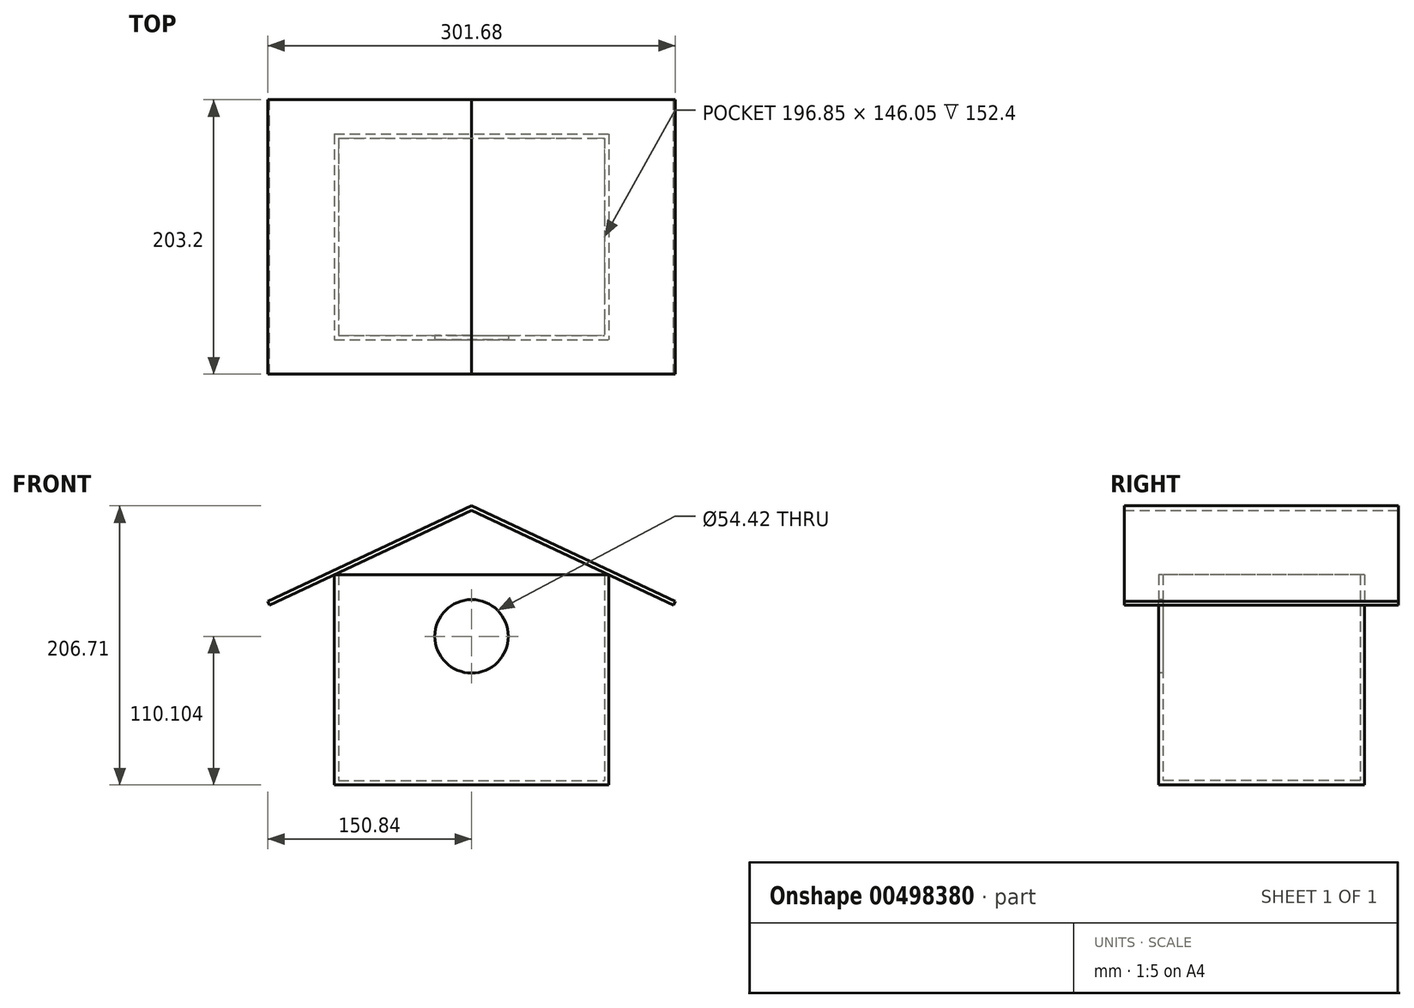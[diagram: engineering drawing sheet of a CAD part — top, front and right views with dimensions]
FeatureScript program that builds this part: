
annotation { "Feature Type Name" : "Feature", "Feature Type Description" : "" }
export const myFeature = defineFeature(function(context is Context, id is Id, definition is map)
    precondition{}
    {
        {
            var Q0;
            Q0=qCreatedBy(makeId("Top.planeOp"),FACE);
            var sketch = newSketch(context, id + "F0", { "sketchPlane" : qUnion([Q0])});
            skLineSegment(sketch, "E0.bottom", {"start": v(-101.6, 76.2) * mm, "end": v(101.6, 76.2) * mm});
            skLineSegment(sketch, "E0.top", {"start": v(-101.6, -76.2) * mm, "end": v(101.6, -76.2) * mm});
            skLineSegment(sketch, "E0.left", {"start": v(-101.6, 76.2) * mm, "end": v(-101.6, -76.2) * mm});
            skLineSegment(sketch, "E0.right", {"start": v(101.6, 76.2) * mm, "end": v(101.6, -76.2) * mm});
            skLineSegment(sketch, "E1", {"start": v(-101.6, 76.2) * mm, "end": v(101.6, -76.2) * mm, "construction": true});
            skSolve(sketch);
        }
        {
            var Q0;
            Q0 = qSketchRegion(id + "F0", true);
            extrude(context, id + "F1", {"entities" : qUnion([Q0]), "depth" : 3.17 * mm});
        }
        {
            var Q0;
            Q0=makeQuery(id+"F1.opExtrude","CAP_FACE",FACE,{"disambiguationData":[OSD([sQuery(id+"F0.wireOp",EDGE,"E0.bottom"),sQuery(id+"F0.wireOp",EDGE,"E0.top"),sQuery(id+"F0.wireOp",EDGE,"E0.left"),sQuery(id+"F0.wireOp",EDGE,"E0.right")])],"isStart":false});
            var sketch = newSketch(context, id + "F2", { "sketchPlane" : qUnion([Q0])});
            skLineSegment(sketch, "E2.bottom", {"start": v(-101.6, 76.2) * mm, "end": v(101.6, 76.2) * mm});
            skLineSegment(sketch, "E2.top", {"start": v(-101.6, -76.2) * mm, "end": v(101.6, -76.2) * mm});
            skLineSegment(sketch, "E2.left", {"start": v(-101.6, 76.2) * mm, "end": v(-101.6, -76.2) * mm});
            skLineSegment(sketch, "E2.right", {"start": v(101.6, 76.2) * mm, "end": v(101.6, -76.2) * mm});
            skLineSegment(sketch, "E3.bottom", {"start": v(-98.42, 73.03) * mm, "end": v(98.42, 73.03) * mm});
            skLineSegment(sketch, "E3.top", {"start": v(-98.42, -73.02) * mm, "end": v(98.42, -73.02) * mm});
            skLineSegment(sketch, "E3.left", {"start": v(-98.42, 73.03) * mm, "end": v(-98.42, -73.02) * mm});
            skLineSegment(sketch, "E3.right", {"start": v(98.42, 73.03) * mm, "end": v(98.42, -73.02) * mm});
            skSolve(sketch);
        }
        {
            var Q0;
            Q0 = qSketchRegion(id + "F2", true);
            extrude(context, id + "F3", {"entities" : qUnion([Q0]), "operationType" : NewBodyOperationType.ADD, "depth" : 152.4 * mm});
        }
        {
            var Q0;
            Q0=qCreatedBy(makeId("Front.planeOp"),FACE);
            var sketch = newSketch(context, id + "F4", { "sketchPlane" : qUnion([Q0])});
            skLineSegment(sketch, "E4", {"start": v(0, 0) * mm, "end": v(0, 203.2) * mm, "construction": true});
            skLineSegment(sketch, "E5", {"start": v(0, 203.2) * mm, "end": v(-149.5, 133.13) * mm});
            skLineSegment(sketch, "E6", {"start": v(0, 203.2) * mm, "end": v(149.5, 133.13) * mm});
            skLineSegment(sketch, "E7", {"start": v(-149.5, 133.13) * mm, "end": v(-150.84, 136) * mm});
            skLineSegment(sketch, "E8", {"start": v(-150.84, 136) * mm, "end": v(0, 206.7) * mm});
            skLineSegment(sketch, "E9", {"start": v(0, 206.7) * mm, "end": v(150.84, 136) * mm});
            skLineSegment(sketch, "E10", {"start": v(150.84, 136) * mm, "end": v(149.5, 133.13) * mm});
            skSolve(sketch);
        }
        {
            var Q0;
            Q0 = qSketchRegion(id + "F4", true);
            extrude(context, id + "F5", {"entities" : qUnion([Q0]), "endBound" : BoundingType.SYMMETRIC, "depth" : 203.2 * mm});
        }
        {
            var Q0;
            Q0=makeQuery(id+"F3.boolean.opBoolean","MERGE",FACE,{"derivedFrom":[makeQuery(id+"F1.opExtrude","SWEPT_FACE",FACE,{"disambiguationData":[OSD([sQuery(id+"F0.wireOp",EDGE,"E0.top")])]}),makeQuery(id+"F3.opExtrude","SWEPT_FACE",FACE,{"disambiguationData":[OSD([sQuery(id+"F2.wireOp",EDGE,"E2.top")])]})]});
            var sketch = newSketch(context, id + "F6", { "sketchPlane" : qUnion([Q0])});
            skCircle(sketch, "E11", {"center": v(0, 110.1) * mm, "radius": 27.21 * mm});
            skSolve(sketch);
        }
        {
            var Q0;
            Q0 = qSketchRegion(id + "F6", true);
            extrude(context, id + "F7", {"entities" : qUnion([Q0]), "operationType" : NewBodyOperationType.REMOVE, "oppositeDirection" : true, "depth" : 25.4 * mm});
        }
    });
